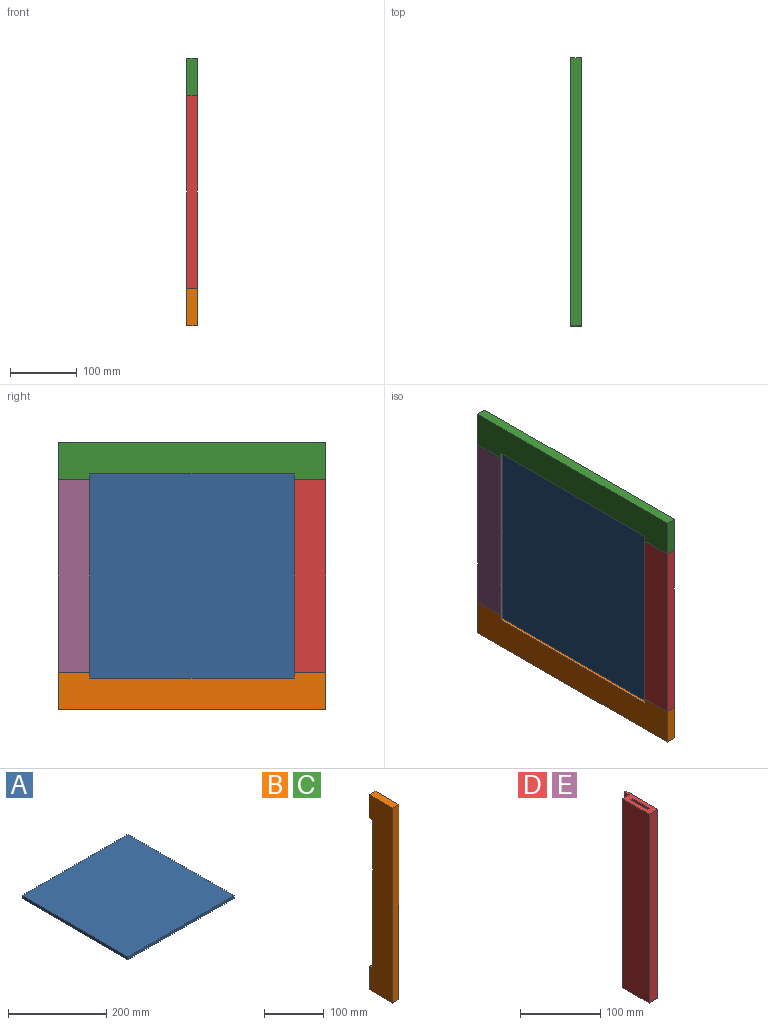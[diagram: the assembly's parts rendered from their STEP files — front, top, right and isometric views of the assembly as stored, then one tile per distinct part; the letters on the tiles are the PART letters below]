
ASSEMBLY  parts=5 mates=12
PART A: 6 faces, bbox 305x305x7 mm
  f0: plane 305x7mm, normal (1,0,0), area 2135mm2, adj f1,f3,f4,f5
  f1: plane 305x7mm, normal (0,1,0), area 2135mm2, adj f0,f2,f4,f5
  f2: plane 305x7mm, normal (-1,0,0), area 2135mm2, adj f1,f3,f4,f5
  f3: plane 305x7mm, normal (0,-1,0), area 2135mm2, adj f0,f2,f4,f5
  f4: plane 305x305mm, normal (0,0,1), area 93025mm2, adj f0,f1,f2,f3
  f5: plane 305x305mm, normal (0,0,-1), area 93025mm2, adj f0,f1,f2,f3
PART B: 20 faces, bbox 15x56x400 mm
  f0: plane 400x15mm, normal (0,1,0), area 2160mm2, adj f1,f2,f4,f5,f6,f7,f9,f10
  f1: plane 400x56mm, normal (-1,0,0), area 19807.5mm2, adj f0,f3,f4,f5,f6,f7,f8
  f2: plane 400x56mm, normal (1,0,0), area 22400mm2, adj f0,f3,f4,f5
  f3: plane 400x15mm, normal (0,-1,0), area 6000mm2, adj f1,f2,f4,f5
  f4: plane 56x15mm, normal (0,0,1), area 840mm2, adj f0,f1,f2,f3
  f5: plane 56x15mm, normal (0,0,-1), area 840mm2, adj f0,f1,f2,f3
  f6: plane 12x8.5mm, normal (0,0,-1), area 102mm2, adj f0,f1,f8,f9
  f7: plane 12x8.5mm, normal (0,0,1), area 102mm2, adj f0,f1,f8,f9
  f8: plane 305x12mm, normal (0,1,0), area 3660mm2, adj f1,f6,f7,f9
  f9: plane 305x8.5mm, normal (-1,0,0), area 2592.5mm2, adj f0,f6,f7,f8
  f10: plane 15x3mm, normal (0,0,-1), area 45mm2, adj f0,f12,f13,f14
  f11: plane 15x3mm, normal (0,0,1), area 45mm2, adj f0,f12,f13,f14
  f12: plane 30x15mm, normal (1,0,0), area 450mm2, adj f0,f10,f11,f14
  f13: plane 30x15mm, normal (-1,0,0), area 450mm2, adj f0,f10,f11,f14
  f14: plane 30x3mm, normal (0,1,0), area 90mm2, adj f10,f11,f12,f13
  f15: plane 15x3mm, normal (0,0,-1), area 45mm2, adj f0,f17,f18,f19
  f16: plane 15x3mm, normal (0,0,1), area 45mm2, adj f0,f17,f18,f19
  f17: plane 30x15mm, normal (1,0,0), area 450mm2, adj f0,f15,f16,f19
  f18: plane 30x15mm, normal (-1,0,0), area 450mm2, adj f0,f15,f16,f19
  f19: plane 30x3mm, normal (0,1,0), area 90mm2, adj f15,f16,f17,f18
PART C: same geometry as B
PART D: 18 faces, bbox 15x56x288 mm
  f0: plane 56x15mm, normal (0,0,-1), area 648mm2, adj f2,f3,f4,f5,f6,f7,f13,f14
  f1: plane 56x15mm, normal (0,0,1), area 648mm2, adj f2,f3,f4,f5,f6,f7,f8,f10
  f2: plane 288x3mm, normal (0,1,0), area 864mm2, adj f0,f1,f4,f6
  f3: plane 288x47.5mm, normal (-1,0,0), area 13680mm2, adj f0,f1,f5,f7
  f4: plane 288x56mm, normal (1,0,0), area 16128mm2, adj f0,f1,f2,f5
  f5: plane 288x15mm, normal (0,-1,0), area 4320mm2, adj f0,f1,f3,f4
  f6: plane 288x8.5mm, normal (-1,0,0), area 2448mm2, adj f0,f1,f2,f7
  f7: plane 288x12mm, normal (0,1,0), area 3456mm2, adj f0,f1,f3,f6
  f8: plane 10x3mm, normal (0,1,0), area 30mm2, adj f1,f9,f11,f12
  f9: plane 30x3mm, normal (0,0,1), area 90mm2, adj f8,f10,f11,f12
  f10: plane 10x3mm, normal (0,-1,0), area 30mm2, adj f1,f9,f11,f12
  f11: plane 30x10mm, normal (1,0,0), area 300mm2, adj f1,f8,f9,f10
  f12: plane 30x10mm, normal (-1,0,0), area 300mm2, adj f1,f8,f9,f10
  f13: plane 10x3mm, normal (0,1,0), area 30mm2, adj f0,f15,f16,f17
  f14: plane 10x3mm, normal (0,-1,0), area 30mm2, adj f0,f15,f16,f17
  f15: plane 30x10mm, normal (1,0,0), area 300mm2, adj f0,f13,f14,f17
  f16: plane 30x10mm, normal (-1,0,0), area 300mm2, adj f0,f13,f14,f17
  f17: plane 30x3mm, normal (0,0,-1), area 90mm2, adj f13,f14,f15,f16
PART E: same geometry as D
PLACE A rot(axis=(-0.58,-0.58,0.58),120deg) t=(160.66,81.78,-405.33)mm
PLACE B rot(axis=(1,0,0),90deg) t=(156.16,81.78,-577.33)mm
PLACE C rot(axis=(-1,0,0),90deg) t=(156.16,81.78,-233.33)mm
PLACE D t=(156.16,-90.22,-405.33)mm
PLACE E rot(axis=(1,0,0),180deg) t=(156.16,253.78,-405.33)mm
MATE planar E.f7 <-> A.f0  axis (0,-1,0) through (154.66,234.28,-405.33)mm
MATE planar E.f0 <-> C.f0  axis (0,0,1) through (156.4,256.93,-261.33)mm
MATE planar A.f1 <-> B.f8  axis (0,0,-1) through (157.16,81.78,-557.83)mm
MATE planar E.f5 <-> B.f5  axis (0,1,0) through (156.16,281.78,-405.33)mm
MATE planar A.f5 <-> C.f9  axis (1,0,0) through (160.66,81.78,-405.33)mm
MATE planar C.f0 <-> D.f1  axis (0,0,-1) through (148.66,-94.47,-261.33)mm
MATE planar C.f5 <-> D.f5  axis (0,-1,0) through (156.16,-118.22,-233.33)mm
MATE planar D.f4 <-> C.f2  axis (1,0,0) through (163.66,-90.22,-405.33)mm
MATE planar E.f5 <-> C.f4  axis (0,1,0) through (156.16,281.78,-405.33)mm
MATE planar E.f4 <-> C.f2  axis (1,0,0) through (163.66,253.78,-405.33)mm
MATE planar B.f0 <-> D.f0  axis (0,0,1) through (158.7,81.78,-549.33)mm
MATE planar C.f2 <-> B.f2  axis (1,0,0) through (163.66,81.78,-233.33)mm
